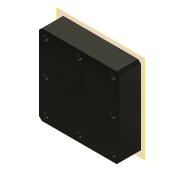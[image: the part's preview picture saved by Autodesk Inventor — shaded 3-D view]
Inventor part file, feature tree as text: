
AUTODESK INVENTOR PART (.ipt)
format: ipt  version: 2019 (Build 230136000, 136)  size: 114,176 bytes
history: native  units: mm
features: other x4, reference x3, sketch x2, plane x1, extrude x1, hole x1
ambient origin geometry x8: Origin, YZ Plane, XZ Plane, XY Plane, X Axis, Y Axis, Z Axis, Center Point
bodies: Solid1 (feature_tree)
feature tree (12):
  plane  "Work Plane1"
  extrude  "Extrusion1"  Depth=50.0mm
  hole  "Hole1"  [1 undecoded]
  sketch  "Sketch1"  dims[d0=50.0mm d1=50.0mm]
  reference  "Reference1"
  sketch  "Sketch2"  dims[d2=16.0mm d3=0.0mm d4=50.0mm d5=50.0mm d6=3.9mm d7=6.0mm d8=4.0mm d9=2.0mm d10=90.0deg d11=10.0mm d12=20.594885mm]
  reference  "Reference2"
  reference  "Reference3"
  other  "00_XY_stage-CHUO_SEIKI_LD-647-R1.iam"
  other  "00_XY_stage-CHUO_SEIKI_LD-647-R1-Middle:1"
  other  "00_XY_stage-CHUO_SEIKI_LD-647-R1-Top:1"
  other  "Assembly2"
note: 1 required parameter value undecoded (feature->parameter linkage not recoverable at this tier; creation-order binding heuristic only, values carry confidence <= 0.55)
